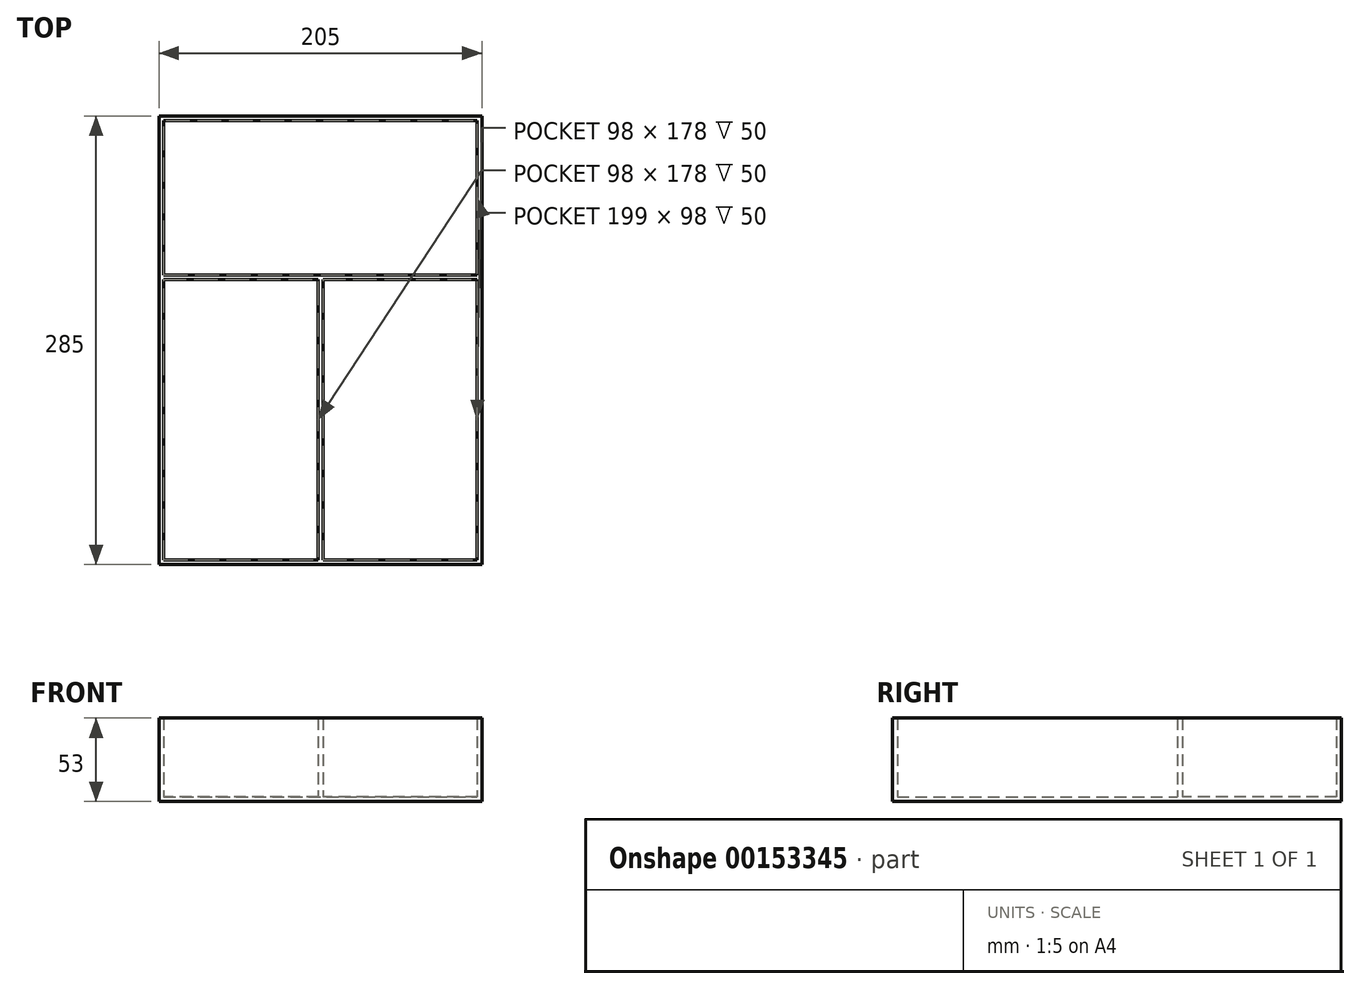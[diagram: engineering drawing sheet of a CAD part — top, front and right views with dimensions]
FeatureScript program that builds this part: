
annotation { "Feature Type Name" : "Feature", "Feature Type Description" : "" }
export const myFeature = defineFeature(function(context is Context, id is Id, definition is map)
    precondition{}
    {
        {
            var Q0;
            Q0=qCreatedBy(makeId("Top.planeOp"),FACE);
            var sketch = newSketch(context, id + "F0", { "sketchPlane" : qUnion([Q0])});
            skLineSegment(sketch, "E0.bottom", {"start": v(102.5, 142.5) * mm, "end": v(-102.5, 142.5) * mm});
            skLineSegment(sketch, "E0.top", {"start": v(102.5, -142.5) * mm, "end": v(-102.5, -142.5) * mm});
            skLineSegment(sketch, "E0.left", {"start": v(102.5, 142.5) * mm, "end": v(102.5, -142.5) * mm});
            skLineSegment(sketch, "E0.right", {"start": v(-102.5, 142.5) * mm, "end": v(-102.5, -142.5) * mm});
            skPoint(sketch, "E0.middle", {"position": v(0, 0) * mm});
            skSolve(sketch);
        }
        {
            var Q0;
            Q0=makeQuery(id+"F0.imprint","IMPRINT",FACE,{"disambiguationData":[TD([[makeQuery(id+"F0.imprint","IMPRINT",EDGE,{"derivedFrom":sQuery(id+"F0.wireOp",EDGE,"E0.bottom")}),1.0]])]});
            extrude(context, id + "F1", {"entities" : qUnion([Q0]), "depth" : 3 * mm});
        }
        {
            var Q0;
            Q0=makeQuery(id+"F1.opExtrude","CAP_FACE",FACE,{"disambiguationData":[OSD([sQuery(id+"F0.wireOp",EDGE,"E0.bottom"),sQuery(id+"F0.wireOp",EDGE,"E0.top"),sQuery(id+"F0.wireOp",EDGE,"E0.left"),sQuery(id+"F0.wireOp",EDGE,"E0.right")])],"isStart":false});
            var sketch = newSketch(context, id + "F2", { "sketchPlane" : qUnion([Q0])});
            skLineSegment(sketch, "E1.0", {"start": v(99.5, 139.5) * mm, "end": v(99.5, -139.5) * mm, "construction": true});
            skLineSegment(sketch, "E1.1", {"start": v(99.5, 139.5) * mm, "end": v(-99.5, 139.5) * mm});
            skLineSegment(sketch, "E1.2", {"start": v(-99.5, 139.5) * mm, "end": v(-99.5, -139.5) * mm, "construction": true});
            skLineSegment(sketch, "E1.3", {"start": v(99.5, -139.5) * mm, "end": v(-99.5, -139.5) * mm});
            skLineSegment(sketch, "E2", {"start": v(0, -139.5) * mm, "end": v(0, 40) * mm, "construction": true});
            skLineSegment(sketch, "E3", {"start": v(0, 40) * mm, "end": v(99.5, 40) * mm, "construction": true});
            skLineSegment(sketch, "E4", {"start": v(0, 40) * mm, "end": v(-99.5, 40) * mm, "construction": true});
            skLineSegment(sketch, "E5.0", {"start": v(-1.5, 38.5) * mm, "end": v(-99.5, 38.5) * mm});
            skLineSegment(sketch, "E5.1", {"start": v(-1.5, -139.5) * mm, "end": v(-1.5, 38.5) * mm});
            skLineSegment(sketch, "E6.0", {"start": v(1.5, 38.5) * mm, "end": v(99.5, 38.5) * mm});
            skLineSegment(sketch, "E6.1", {"start": v(1.5, -139.5) * mm, "end": v(1.5, 38.5) * mm});
            skLineSegment(sketch, "E7.0", {"start": v(0, 41.5) * mm, "end": v(99.5, 41.5) * mm});
            skLineSegment(sketch, "E7.1", {"start": v(0, 41.5) * mm, "end": v(-99.5, 41.5) * mm});
            skLineSegment(sketch, "E8", {"start": v(-99.5, 139.5) * mm, "end": v(-99.5, 41.5) * mm});
            skLineSegment(sketch, "E9", {"start": v(99.5, 139.5) * mm, "end": v(99.5, 41.5) * mm});
            skLineSegment(sketch, "E10", {"start": v(99.5, -139.5) * mm, "end": v(99.5, 38.5) * mm});
            skLineSegment(sketch, "E11", {"start": v(-99.5, 38.5) * mm, "end": v(-99.5, -139.5) * mm});
            skSolve(sketch);
        }
        {
            var Q0;
            Q0=makeQuery(id+"F2.imprint","IMPRINT",FACE,{"disambiguationData":[TD([[makeQuery(id+"F2.imprint","IMPRINT",EDGE,{"derivedFrom":sQuery(id+"F2.wireOp",EDGE,"E1.1")}),-1.0]])]});
            extrude(context, id + "F3", {"entities" : qUnion([Q0]), "operationType" : NewBodyOperationType.ADD, "depth" : 50 * mm});
        }
    });
